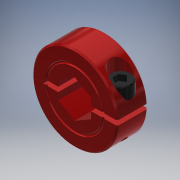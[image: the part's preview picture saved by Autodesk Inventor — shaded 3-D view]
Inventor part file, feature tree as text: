
AUTODESK INVENTOR PART (.ipt)
format: ipt  version: 2017.1 (Build 211199000, 199)  size: 303,104 bytes
history: native  units: in
note: dims shown in document units (in); Inventor stores cm internally (conversion verified against a paired STEP export)
features: extrude x2, sketch x2, other x1, imported_body x1
ambient origin geometry x8: Origin, YZ Plane, XZ Plane, XY Plane, X Axis, Y Axis, Z Axis, Center Point
bodies: Solid1 (feature_tree)
feature tree (6):
  other  "CL-8-A1"
  extrude  "Extrusion1"  Depth=0.4375in TaperAngle=0.0deg
  extrude  "Extrusion2"  [1 undecoded]
  imported_body  "Base1"
  sketch  "Sketch2"  dims[d0=0.5in d1=0.4375in d2=0.0in]
  sketch  "Sketch3"  dims[d3=1.0in d4=0.0in]
note: 1 required parameter value undecoded (feature->parameter linkage not recoverable at this tier; creation-order binding heuristic only, values carry confidence <= 0.55)
